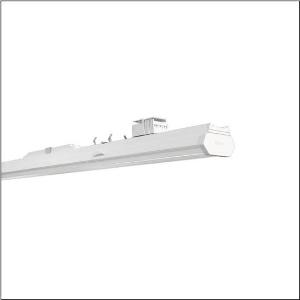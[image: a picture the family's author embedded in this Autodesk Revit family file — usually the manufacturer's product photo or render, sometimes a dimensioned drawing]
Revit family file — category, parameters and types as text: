
# Revit family: licross_r__11_protected_ho_51tp13cn4e5s_b79e
name_source: partatom
category: Lighting Fixtures
units: mm (PartAtom-declared; Revit-internal decimal feet)

## family parameters
Cut with Voids When Loaded = No
Host = Face
Light Source = No
Part Type = Normal
Room Calculation Point = No
Round Connector Dimension = Use Diameter
Shared = No

## types (1)
- --- (1 x LED, 14500 lm, 77.6 W, 4000K)
    Apparent Load = 78 VA
    CIE Flux Codes = 89 96 99 100 99
    Color Rendering = 80
    Color Temperature = 4000K
    Default Elevation = 1800 mm
    Description = Licross® 11 Protected HO, luminaire insert, of sheet steel, galvanised, coil coated, white, length: 1.500mm, width: 90mm, height: 101mm, LED rated luminous flux: 14.500lm, light colour: 840, control gear: ON/OFF Multilumen, CLOi, with plug, 3-pole, with phase selection, mains connection: 220..240V, AC, 50/60Hz, start of lifetime: 78W, end of service life: 87W, halogen-free wiring, primary light control with lens, of plastic, primary optical cover: cover, of PMMA, light emission: direct distribution, primary light characteristic: symmetric, protection rating (complete): IP64, insulation class (complete): insulation class I (protective earthing), certification: CE, ENEC, VDE, UKCA, protection symbol: D if used in an environment with conductive dust loads with corresponding accessories, impact resistance: IK06, permissible ambient temperature for indoor applications: -35..+35°C, corresponds to IFS (International Featured Standards) requirements for safety and quality in the food industry, reducing of maximum allowable ambient temperature of 5°C with ceiling mounting, LABS conformity tested according to VDMA 24364:2018-05, packaging unit: 1 piece
    Height = 92 mm
    Lamp = 1 x LED
    Lamp Light Flux = 14500 lm
    Lamp Power = 77.6 W
    Lamp count = 1
    Length = 1500 mm
    Luminous efficacy = 187 lm/W
    Manufacturer = Siteco
    ModVariant = No
    Model = 51TP13CN4E5S
    Mounting Place = Ceiling
    Mounting Type = Pendant
    Number of Poles = 1
    OnlyDefault = Yes
    Power Factor = 1
    Product Name = Licross® 11 Protected HO
    Product group = luminaire insert
    ProductGroupID = 901
    Protection Class = Protection class I
    Protection Degree = IP 64
    RLX_Detail_Level = 1
    RLX_Emergency_Light_Flux = 0 lm
    RLX_Emergency_Type = 0
    RLX_Emergency_Type_DB = No
    RlxData = <blob elided: 22113 chars, md5=b3366c28>
    Socket = socket
    Standby Power = 0 W
    System Light Flux = 14500 lm
    System Power = 78 W
    Type Comments = factory setting: luminous flux: 100 % | (A | C | E) | 181 mA
    Type Image = l_1256148.jpg
    URL = http://relux.com
    VarID = @adj_055039
    Voltage = 0 V
    Weight = 0.00 kg
    Width = 88 mm

## geometry (parser evidence)
native form markers: Blend x4, Sweep x12
no freeform markers — native parametric forms only
